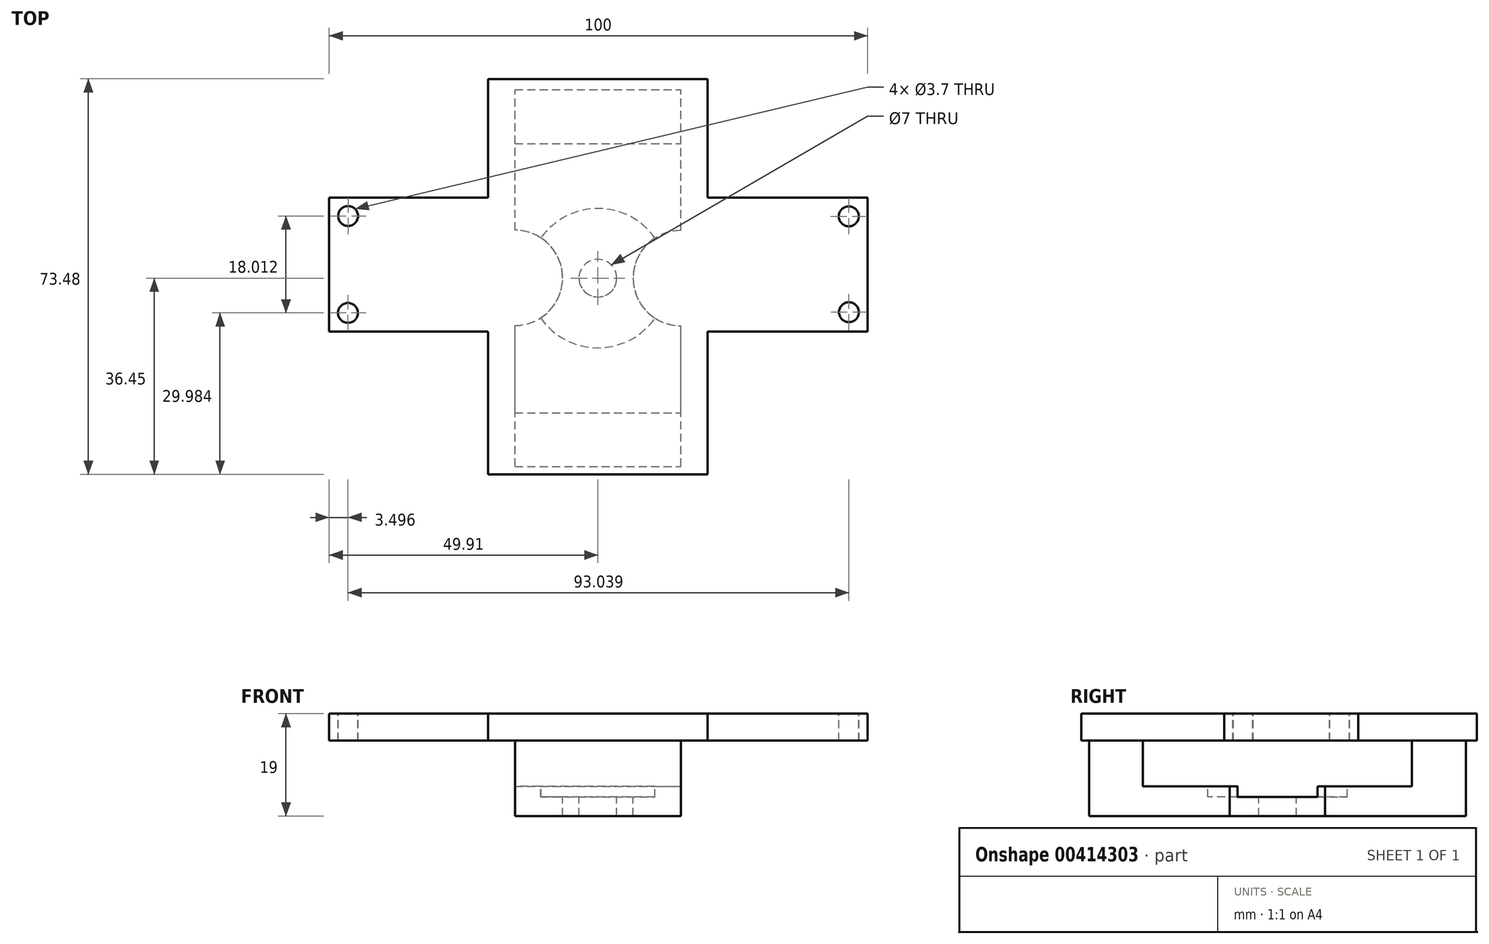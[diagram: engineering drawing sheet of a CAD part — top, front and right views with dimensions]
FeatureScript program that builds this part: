
annotation { "Feature Type Name" : "Feature", "Feature Type Description" : "" }
export const myFeature = defineFeature(function(context is Context, id is Id, definition is map)
    precondition{}
    {
        {
            var Q0;
            Q0=qCreatedBy(makeId("Top.planeOp"),FACE);
            var sketch = newSketch(context, id + "F0", { "sketchPlane" : qUnion([Q0])});
            skLineSegment(sketch, "E0.0", {"start": v(-15.4, 53.06) * mm, "end": v(-15.4, -20.42) * mm});
            skLineSegment(sketch, "E0.1", {"start": v(25.36, 53.06) * mm, "end": v(-15.4, 53.06) * mm});
            skLineSegment(sketch, "E0.2", {"start": v(25.36, -20.42) * mm, "end": v(25.36, 53.06) * mm});
            skLineSegment(sketch, "E0.3", {"start": v(-15.4, -20.42) * mm, "end": v(25.36, -20.42) * mm});
            skSolve(sketch);
        }
        {
            var Q0;
            Q0=makeQuery(id+"F0.imprint","IMPRINT",FACE,{"disambiguationData":[TD([[makeQuery(id+"F0.imprint","IMPRINT",EDGE,{"derivedFrom":sQuery(id+"F0.wireOp",EDGE,"E0.0")}),1.0]])]});
            extrude(context, id + "F1", {"entities" : qUnion([Q0]), "oppositeDirection" : true, "depth" : 5 * mm});
        }
        {
            var Q0;
            Q0=makeQuery(id+"F1.opExtrude","CAP_FACE",FACE,{"disambiguationData":[OSD([sQuery(id+"F0.wireOp",EDGE,"E0.0"),sQuery(id+"F0.wireOp",EDGE,"E0.1"),sQuery(id+"F0.wireOp",EDGE,"E0.2"),sQuery(id+"F0.wireOp",EDGE,"E0.3"),sQuery(id+"F0.wireOp",EDGE,"AwGas1L0-Tx7c-sK6K-lToC-j4NMW9GVDTDE.right")])],"isStart":false});
            var sketch = newSketch(context, id + "F2", { "sketchPlane" : qUnion([Q0])});
            skLineSegment(sketch, "E1.bottom", {"start": v(-10.4, 18.97) * mm, "end": v(20.4, 18.97) * mm});
            skLineSegment(sketch, "E1.top", {"start": v(-10.4, -51.03) * mm, "end": v(20.4, -51.03) * mm});
            skLineSegment(sketch, "E1.left", {"start": v(-10.4, 18.97) * mm, "end": v(-10.4, -7.23) * mm});
            skLineSegment(sketch, "E1.right", {"start": v(20.4, 18.97) * mm, "end": v(20.4, -7.18) * mm});
            skCircle(sketch, "E2", {"center": v(5, -16.03) * mm, "radius": 3.5 * mm});
            skArc(sketch, "E3", {"start": v(20.4, -7.18) * mm, "mid": v(11.55, -16.03) * mm, "end": v(20.4, -24.88) * mm});
            skArc(sketch, "E4", {"start": v(-10.4, -24.93) * mm, "mid": v(-1.55, -16.08) * mm, "end": v(-10.4, -7.23) * mm});
            skLineSegment(sketch, "E5.trimOffspring", {"start": v(-10.4, -16.03) * mm, "end": v(-10.4, -16.08) * mm});
            skLineSegment(sketch, "E6.trimOffspring", {"start": v(-10.4, -24.93) * mm, "end": v(-10.4, -51.03) * mm});
            skLineSegment(sketch, "E7.trimOffspring", {"start": v(20.4, -24.88) * mm, "end": v(20.4, -51.03) * mm});
            skSolve(sketch);
        }
        {
            var Q0;
            Q0=qSketchRegion(id+"F2",true);
            extrude(context, id + "F3", {"entities" : qUnion([Q0]), "operationType" : NewBodyOperationType.ADD, "depth" : 14 * mm});
        }
        {
            var Q0;
            {var subQ0=sQuery(id+"F0.wireOp",EDGE,"AwGas1L0-Tx7c-sK6K-lToC-j4NMW9GVDTDE.right");var subQ1=sQuery(id+"F0.wireOp",EDGE,"E0.0");var subQ2=sQuery(id+"F0.wireOp",EDGE,"E0.1");var subQ3=sQuery(id+"F0.wireOp",EDGE,"E0.2");var subQ4=sQuery(id+"F0.wireOp",EDGE,"E0.3");Q0=makeQuery(id+"F3.boolean.opBoolean","SPLIT",FACE,{"disambiguationData":[TD([makeQuery(id+"F1.opExtrude","SWEPT_FACE",FACE,{"disambiguationData":[OSD([subQ2])]})])],"derivedFrom":makeQuery(id+"F1.opExtrude","CAP_FACE",FACE,{"disambiguationData":[OSD([subQ1,subQ2,subQ3,subQ4,subQ0])],"isStart":false})});}
            var sketch = newSketch(context, id + "F4", { "sketchPlane" : qUnion([Q0])});
            skLineSegment(sketch, "E8.bottom", {"start": v(-14.6, 9.01) * mm, "end": v(20.4, 9.01) * mm});
            skLineSegment(sketch, "E8.top", {"start": v(-14.6, -41) * mm, "end": v(20.4, -41) * mm});
            skLineSegment(sketch, "E8.left", {"start": v(-14.6, 9.01) * mm, "end": v(-14.6, -41) * mm});
            skLineSegment(sketch, "E8.right", {"start": v(20.4, 9.01) * mm, "end": v(20.4, -41) * mm});
            skSolve(sketch);
        }
        {
            var Q0;
            Q0=qSketchRegion(id+"F4",true);
            var Q1;
            Q1=sQuery(id+"F4.wireOp",EDGE,"E8.left");
            extrude(context, id + "F5", {"entities" : qUnion([Q0]), "operationType" : NewBodyOperationType.REMOVE, "surfaceEntities" : qUnion([Q1]), "depth" : 8.5 * mm});
        }
        {
            var Q0;
            {var subQ0=sQuery(id+"F0.wireOp",EDGE,"E0.3");var subQ1=sQuery(id+"F0.wireOp",EDGE,"E0.2");var subQ2=sQuery(id+"F0.wireOp",EDGE,"E0.1");var subQ3=sQuery(id+"F0.wireOp",EDGE,"E0.0");var subQ4=makeQuery(id+"F1.opExtrude","CAP_FACE",FACE,{"disambiguationData":[OSD([subQ3,subQ2,subQ1,subQ0])],"isStart":false});Q0=makeQuery(id+"F5.boolean.opBoolean","MERGE",FACE,{"derivedFrom":[makeQuery(id+"F3.boolean.opBoolean","SPLIT",FACE,{"disambiguationData":[TD([makeQuery(id+"F1.opExtrude","SWEPT_FACE",FACE,{"disambiguationData":[OSD([subQ3])]})])],"derivedFrom":subQ4}),makeQuery(id+"F3.boolean.opBoolean","SPLIT",FACE,{"disambiguationData":[TD([makeQuery(id+"F3.opExtrude","SWEPT_FACE",FACE,{"disambiguationData":[OSD([sQuery(id+"F2.wireOp",EDGE,"wV9iuwiv-zcHe-cE0k-HwwL-fQ0fSy19g1jQ")])]})])],"derivedFrom":subQ4}),makeQuery(id+"F3.boolean.opBoolean","SPLIT",FACE,{"disambiguationData":[TD([makeQuery(id+"F3.opExtrude","SWEPT_FACE",FACE,{"disambiguationData":[OSD([sQuery(id+"F2.wireOp",EDGE,"v6R7sFhp-tAEI-SnQt-5ool-xOl96yPjNEbj")])]})])],"derivedFrom":subQ4}),makeQuery(id+"F5.opExtrude","CAP_FACE",FACE,{"disambiguationData":[OSD([sQuery(id+"F4.wireOp",EDGE,"E8.bottom"),sQuery(id+"F4.wireOp",EDGE,"E8.top"),sQuery(id+"F4.wireOp",EDGE,"E8.left"),sQuery(id+"F4.wireOp",EDGE,"E8.right")])],"isStart":true})]});}
            var sketch = newSketch(context, id + "F6", { "sketchPlane" : qUnion([Q0])});
            skLineSegment(sketch, "E9.bottom", {"start": v(-44.9, -31.01) * mm, "end": v(55.1, -31.01) * mm});
            skLineSegment(sketch, "E9.top", {"start": v(-44.9, -6.1) * mm, "end": v(55.1, -6.1) * mm});
            skLineSegment(sketch, "E9.left", {"start": v(-44.9, -31.01) * mm, "end": v(-44.9, -6.1) * mm});
            skLineSegment(sketch, "E9.right", {"start": v(55.1, -31.01) * mm, "end": v(55.1, -6.1) * mm});
            skPoint(sketch, "E10.endSnap0", {"position": v(4.98, -53.06) * mm});
            skSolve(sketch);
        }
        {
            var Q0;
            Q0=qSketchRegion(id+"F6",true);
            extrude(context, id + "F7", {"entities" : qUnion([Q0]), "operationType" : NewBodyOperationType.ADD, "oppositeDirection" : true, "depth" : 5 * mm});
        }
        {
            var Q0;
            Q0=makeQuery(id+"F7.boolean.opBoolean","MERGE",FACE,{"derivedFrom":[makeQuery(id+"F1.opExtrude","CAP_FACE",FACE,{"disambiguationData":[OSD([sQuery(id+"F0.wireOp",EDGE,"E0.0"),sQuery(id+"F0.wireOp",EDGE,"E0.1"),sQuery(id+"F0.wireOp",EDGE,"E0.2"),sQuery(id+"F0.wireOp",EDGE,"E0.3")])],"isStart":true}),makeQuery(id+"F7.opExtrude","CAP_FACE",FACE,{"disambiguationData":[OSD([sQuery(id+"F6.wireOp",EDGE,"E9.bottom"),sQuery(id+"F6.wireOp",EDGE,"E9.top"),sQuery(id+"F6.wireOp",EDGE,"E9.left"),sQuery(id+"F6.wireOp",EDGE,"E9.right")])],"isStart":false})]});
            var sketch = newSketch(context, id + "F8", { "sketchPlane" : qUnion([Q0])});
            skCircle(sketch, "E11", {"center": v(-41.39, 27.58) * mm, "radius": 1.85 * mm});
            skCircle(sketch, "E12", {"center": v(51.6, 27.51) * mm, "radius": 1.85 * mm});
            skLineSegment(sketch, "E13", {"start": v(-44.9, 31.01) * mm, "end": v(-41.4, 31.01) * mm});
            skCircle(sketch, "E14", {"center": v(-41.41, 9.56) * mm, "radius": 1.85 * mm});
            skCircle(sketch, "E15", {"center": v(51.62, 9.7) * mm, "radius": 1.85 * mm});
            skSolve(sketch);
        }
        {
            var Q0;
            Q0=qSketchRegion(id+"F8",true);
            extrude(context, id + "F9", {"entities" : qUnion([Q0]), "operationType" : NewBodyOperationType.REMOVE, "oppositeDirection" : true, "depth" : 25.4 * mm});
        }
        {
            var Q0;
            Q0=makeQuery(id+"F5.boolean.opBoolean","COPY",FACE,{"derivedFrom":makeQuery(id+"F5.opExtrude","CAP_FACE",FACE,{"disambiguationData":[OSD([sQuery(id+"F4.wireOp",EDGE,"E8.bottom"),sQuery(id+"F4.wireOp",EDGE,"E8.top"),sQuery(id+"F4.wireOp",EDGE,"E8.left"),sQuery(id+"F4.wireOp",EDGE,"E8.right")])],"isStart":false})});
            var sketch = newSketch(context, id + "F10", { "sketchPlane" : qUnion([Q0])});
            skCircle(sketch, "E16", {"center": v(5, 16.03) * mm, "radius": 12.95 * mm});
            skSolve(sketch);
        }
        {
            var Q0;
            Q0=qSketchRegion(id+"F10",true);
            extrude(context, id + "F11", {"entities" : qUnion([Q0]), "operationType" : NewBodyOperationType.REMOVE, "oppositeDirection" : true, "depth" : 2 * mm});
        }
    });
